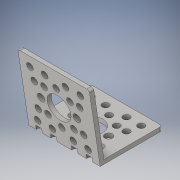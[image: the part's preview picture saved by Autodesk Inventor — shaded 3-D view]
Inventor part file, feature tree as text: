
AUTODESK INVENTOR PART (.ipt)
format: ipt  version: 2016 (Build 200138000, 138)  size: 253,952 bytes
history: native  units: in
note: dims shown in document units (in); Inventor stores cm internally (conversion verified against a paired STEP export)
features: direct_edit x1, fillet x1, revolve x1
ambient origin geometry x8: Origin, YZ Plane, XZ Plane, XY Plane, X Axis, Y Axis, Z Axis, Center Point
bodies: Solid1 (feature_tree)
feature tree (3):
  direct_edit  "Direct Edit1"
  fillet  "Fillet1"  Radius=0.0602in
  revolve  "Rotate1"  [1 undecoded]
note: 1 required parameter value undecoded (feature->parameter linkage not recoverable at this tier; creation-order binding heuristic only, values carry confidence <= 0.55)
